# Revit family: Haworth_Janus_Matisse_StraightLoungeModule_NA
name_source: partatom
category: Furniture
units: mm (PartAtom-declared; Revit-internal decimal feet)

## family parameters
Always vertical = Yes
Cut with Voids When Loaded = No
OmniClass Number = 23.40.70.14.64.11
OmniClass Title = Office Furniture
Room Calculation Point = No
Shared = No
Work Plane-Based = No

## types (6) — shared parameters
Actual Depth = 32 3/4"
Actual Height = 34 1/2"
Assembly Code = E2020200
Description = Haworth - Janus - Matisse - Straight Lounge Module
Manufacturer = Haworth
Model = Haworth - Janus - Matisse
Note = Verify Final Dim. w/ Haworth
Revision Number = 1
URL = https://www.haworth.com

## per-type parameters (varying)
| type | Actual Width | Left Arm | Left Offset for Arm | Right Arm | Right Offset for Arm | Seat Width | Total Arm Width |
| Lounge Chair | 31 1/2" | Yes | 3" | Yes | 3" | 25 1/2" | 6" |
| 2-Seat Sofa | 56 3/4" | Yes | 3" | Yes | 3" | 50 3/4" | 6" |
| 1-Seat Module without Arms | 25 1/4" | No | 0" | No | 0" | 25 1/4" | 0" |
| Wide 1-Seat Module without Arms | 36 1/4" | No | 0" | No | 0" | 36 1/4" | 0" |
| 2-Seat Module with Left Arm | 53 1/2" | Yes | 3" | No | 0" | 50 1/2" | 3" |
| 2-Seat Module with Right Arm | 53 1/2" | No | 0" | Yes | 3" | 50 1/2" | 3" |

## geometry (parser evidence)
native form markers: Sweep x6
no freeform markers — native parametric forms only
